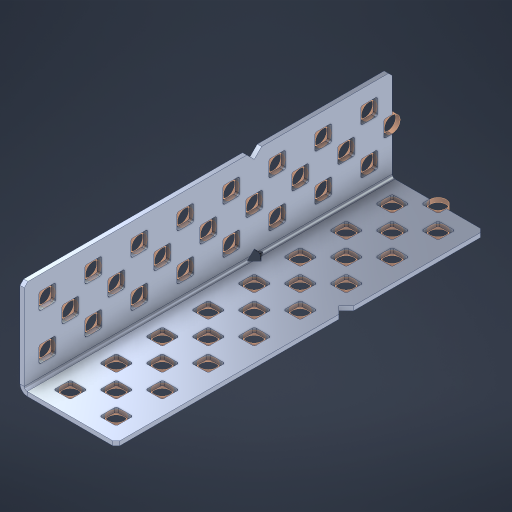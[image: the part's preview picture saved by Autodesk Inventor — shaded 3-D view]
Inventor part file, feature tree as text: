
AUTODESK INVENTOR PART (.ipt)
format: ipt  version: 2023 (Build 270158000, 158)  size: 847,360 bytes
history: native  units: in
note: dims shown in document units (in); Inventor stores cm internally (conversion verified against a paired STEP export)
features: other x54, extrude x46, sheet_metal_op x8, sketch x7, pattern_linear x2, mirror x1, chamfer x1
ambient origin geometry x8: Origin, YZ Plane, XZ Plane, XY Plane, X Axis, Y Axis, Z Axis, Center Point
bodies: Solid1 (feature_tree), Body (feature_tree)
feature tree (119):
  sheet_metal_op  "Flanges"
  sheet_metal_op  "Body Pattern"
  pattern_linear  "Center Pattern"  Spacing1=1.0in  [1 undecoded]
  other  "Arc Length"
  pattern_linear  "Notch Pattern"  Spacing1=0.1875in  [1 undecoded]
  other  "Diagonal Plane"
  mirror  "Everything Mirrored"
  chamfer  "End Chamfer"
  sketch  "Sketch1"  dims[d0=1.0in]
  other  "Plate1"
  sketch  "Sketch2"  dims[d1=4.0in]
  other  "Plate2"
  sheet_metal_op  "Bend1"
  sheet_metal_op  "Corner1"
  sketch  "Sketch8"  dims[d2=0.0469in]
  sketch  "Sketch9"  dims[d3=0.0469in]
  other  "Srf91"
  sheet_metal_op  "Body Pattern Sketch"
  other  "Srf92"
  sketch  "Sketch13"  dims[d4=0.0234in]
  sketch  "Sketch15"  dims[d5=0.0938in]
  sketch  "Sketch16"  dims[d6=0.0469in d7=1.0in d8=90.0deg d9=0.0312in d10=0.1875in d11=0.0469in d12=0.0469in d49=0.182in d50=0.02in d52=0.25in d53=0.0469in d54=0.0in d55=0.172in d56=1.0in d57=0.0in d60=3.1496in d62=0.5in d63=0.7874in d65=0.5in d85=0.1473in d86=0.1659in d89=0.0469in d90=0.0in d91=0.04in d92=0.0491in d95=2.5in d96=0.04in d97=0.25in d98=45.0deg d99=0.25in d106=0.182in d107=0.02in d108=0.5in d110=0.0469in d111=0.0in d112=0.172in d113=0.5in d114=0.0in d117=0.5in d123=0.25in d125=0.25in d126=0.0491in d127=0.1227in d128=0.08in d129=0.04in d130=2.5in]
  other  "Srf786"
  other  "Srf856"
  other  "Srf857"
  other  "Srf858"
  other  "Srf859"
  other  "Srf860"
  other  "Srf861"
  other  "Srf889"
  other  "Srf890"
  other  "Srf891"
  other  "Srf1275"
  other  "Srf1276"
  other  "Srf1278"
  other  "Srf1279"
  other  "Srf1280"
  other  "Srf1281"
  other  "Srf1282"
  other  "Srf1283"
  other  "Srf1277"
  other  "Srf1285"
  other  "Srf1286"
  other  "Srf1287"
  other  "Srf1383"
  other  "Srf1384"
  other  "Srf1385"
  other  "Srf1386"
  other  "Srf1387"
  other  "Srf1388"
  other  "Srf1389"
  other  "Srf1390"
  other  "Srf1445"
  other  "Srf1446"
  other  "Srf1447"
  other  "Srf1448"
  other  "Srf1475"
  other  "Srf1476"
  other  "Srf1477"
  other  "Srf1478"
  other  "Srf1479"
  other  "Srf1480"
  other  "Srf1481"
  other  "Srf1482"
  other  "Srf1537"
  other  "Srf1538"
  other  "Srf1539"
  other  "Srf1540"
  sheet_metal_op  "Body Stamp"
  sheet_metal_op  "Body Circle"
  other  "Center Stamp"
  other  "Center Circle"
  sheet_metal_op  "Notch"
  extrude  "ExtrusionSrf92"  Depth=0.0469in
  extrude  "ExtrusionSrf856"  Depth=0.0469in
  extrude  "ExtrusionSrf857"  Depth=0.182in
  extrude  "ExtrusionSrf858"  Depth=0.02in
  extrude  "ExtrusionSrf859"  Depth=0.25in
  extrude  "ExtrusionSrf860"  Depth=0.0469in
  extrude  "ExtrusionSrf861"  TaperAngle=0.0deg  [1 undecoded]
  extrude  "ExtrusionSrf889"  Depth=2.5in
  extrude  "ExtrusionSrf890"  Depth=1.0in TaperAngle=0.0deg
  extrude  "ExtrusionSrf891"  Depth=2.5in
  extrude  "ExtrusionSrf1275"  Depth=0.5in
  extrude  "ExtrusionSrf1276"  Depth=2.5in
  extrude  "ExtrusionSrf1277"  Depth=2.5in
  extrude  "ExtrusionSrf1278"  Depth=0.0469in
  extrude  "ExtrusionSrf1279"  Depth=2.5in TaperAngle=0.0deg
  extrude  "ExtrusionSrf1280"  Depth=2.5in
  extrude  "ExtrusionSrf1281"  Depth=0.25in TaperAngle=45.0deg
  extrude  "ExtrusionSrf1282"  Depth=0.25in
  extrude  "ExtrusionSrf1345"  Depth=0.182in
  extrude  "ExtrusionSrf1346"  Depth=0.02in
  extrude  "ExtrusionSrf1347"  Depth=0.5in
  extrude  "ExtrusionSrf1348"  Depth=0.0469in
  extrude  "ExtrusionSrf1383"  TaperAngle=0.0deg  [1 undecoded]
  extrude  "ExtrusionSrf1384"  Depth=2.5in
  extrude  "ExtrusionSrf1385"  Depth=0.5in TaperAngle=0.0deg
  extrude  "ExtrusionSrf1386"  Depth=0.5in
  extrude  "ExtrusionSrf1387"  Depth=0.25in
  extrude  "ExtrusionSrf1388"  Depth=0.25in
  extrude  "ExtrusionSrf1389"  Depth=2.5in
  extrude  "ExtrusionSrf1390"  Depth=2.5in
  extrude  "ExtrusionSrf1445"  Depth=2.5in
  extrude  "ExtrusionSrf1446"  Depth=2.5in
  extrude  "ExtrusionSrf1447"  Depth=2.5in
  extrude  "ExtrusionSrf1448"  [1 undecoded]
  extrude  "ExtrusionSrf1475"  [1 undecoded]
  extrude  "ExtrusionSrf1476"  [1 undecoded]
  extrude  "ExtrusionSrf1477"  [1 undecoded]
  extrude  "ExtrusionSrf1478"  [1 undecoded]
  extrude  "ExtrusionSrf1479"  [1 undecoded]
  extrude  "ExtrusionSrf1480"  [1 undecoded]
  extrude  "ExtrusionSrf1481"  [1 undecoded]
  extrude  "ExtrusionSrf1482"  [1 undecoded]
  extrude  "ExtrusionSrf1537"  [1 undecoded]
  extrude  "ExtrusionSrf1538"  [1 undecoded]
  extrude  "ExtrusionSrf1539"  [1 undecoded]
  extrude  "ExtrusionSrf1540"  [1 undecoded]
note: 17 required parameter values undecoded (feature->parameter linkage not recoverable at this tier; creation-order binding heuristic only, values carry confidence <= 0.55)
